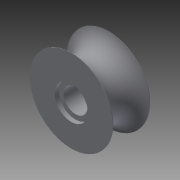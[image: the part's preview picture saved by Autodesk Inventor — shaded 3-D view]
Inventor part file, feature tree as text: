
AUTODESK INVENTOR PART (.ipt)
format: ipt  version: 2015 (Build 190159000, 159)  size: 153,600 bytes
history: native  units: in
note: dims shown in document units (in); Inventor stores cm internally (conversion verified against a paired STEP export)
features: sketch x4, revolve x2, extrude x2
ambient origin geometry x8: Origin, YZ Plane, XZ Plane, XY Plane, X Axis, Y Axis, Z Axis, Center Point
bodies: Solid1 (feature_tree)
feature tree (8):
  revolve  "Revolution1"  [1 undecoded]
  extrude  "Extrusion1"  Depth=0.4882in
  revolve  "Revolution2"  Angle=90.0deg
  extrude  "Extrusion3"  [1 undecoded]
  sketch  "Sketch1"  dims[d0=90.0deg d1=0.3125in]
  sketch  "Sketch2"  dims[d2=1.0in d3=0.0in d4=0.4882in]
  sketch  "Sketch4"  dims[d5=0.6in d9=90.0deg]
  sketch  "Sketch5"  dims[d10=0.0551in d11=0.0in]
note: 2 required parameter values undecoded (feature->parameter linkage not recoverable at this tier; creation-order binding heuristic only, values carry confidence <= 0.55)